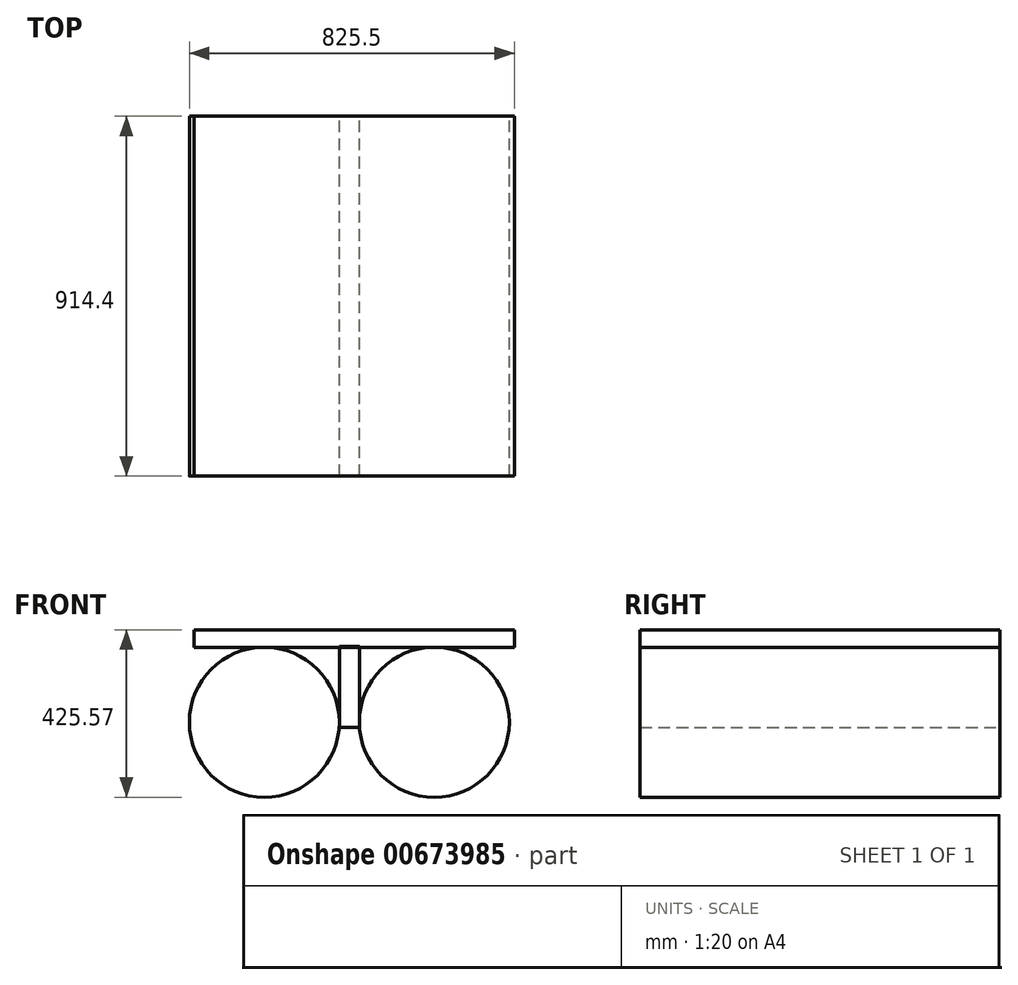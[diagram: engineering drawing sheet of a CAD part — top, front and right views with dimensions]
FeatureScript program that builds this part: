
annotation { "Feature Type Name" : "Feature", "Feature Type Description" : "" }
export const myFeature = defineFeature(function(context is Context, id is Id, definition is map)
    precondition{}
    {
        {
            var Q0;
            Q0=qCreatedBy(makeId("Front.planeOp"),FACE);
            var sketch = newSketch(context, id + "F0", { "sketchPlane" : qUnion([Q0])});
            skLineSegment(sketch, "E0.bottom", {"start": v(-192.12, 42.29) * mm, "end": v(620.68, 42.29) * mm});
            skLineSegment(sketch, "E0.top", {"start": v(-192.12, -2.28) * mm, "end": v(620.68, -2.28) * mm});
            skLineSegment(sketch, "E0.left", {"start": v(-192.12, 42.29) * mm, "end": v(-192.12, -2.28) * mm});
            skLineSegment(sketch, "E0.right", {"start": v(620.68, 42.29) * mm, "end": v(620.68, -2.28) * mm});
            skCircle(sketch, "E1", {"center": v(417.48, -192.78) * mm, "radius": 190.5 * mm});
            skSolve(sketch);
        }
        {
            var Q0;
            Q0=qCreatedBy(makeId("Front.planeOp"),FACE);
            var sketch = newSketch(context, id + "F1", { "sketchPlane" : qUnion([Q0])});
            skLineSegment(sketch, "E2.bottom", {"start": v(226.98, 0) * mm, "end": v(176.18, 0) * mm});
            skLineSegment(sketch, "E2.top", {"start": v(226.98, -205.48) * mm, "end": v(176.18, -205.48) * mm});
            skLineSegment(sketch, "E2.left", {"start": v(226.98, 0) * mm, "end": v(226.98, -205.48) * mm});
            skLineSegment(sketch, "E2.right", {"start": v(176.18, 0) * mm, "end": v(176.18, -205.48) * mm});
            skSolve(sketch);
        }
        {
            var Q0;
            Q0=qCreatedBy(makeId("Front.planeOp"),FACE);
            var sketch = newSketch(context, id + "F2", { "sketchPlane" : qUnion([Q0])});
            skCircle(sketch, "E3", {"center": v(-14.32, -192.78) * mm, "radius": 190.5 * mm});
            skSolve(sketch);
        }
        {
            var Q0;
            Q0 = qSketchRegion(id + "F0", true);
            var Q1;
            Q1=makeQuery(id+"F2.imprint","IMPRINT",FACE,{"disambiguationData":[TD([[makeQuery(id+"F2.imprint","IMPRINT",EDGE,{"derivedFrom":sQuery(id+"F2.wireOp",EDGE,"E3")}),1.0]])]});
            var Q2;
            Q2=makeQuery(id+"F1.imprint","IMPRINT",FACE,{"disambiguationData":[TD([[makeQuery(id+"F1.imprint","IMPRINT",EDGE,{"derivedFrom":sQuery(id+"F1.wireOp",EDGE,"E2.bottom")}),1.0]])]});
            extrude(context, id + "F3", {"entities" : qUnion([Q0, Q1, Q2]), "depth" : 914.4 * mm, "offsetDistance" : 25.4 * mm});
        }
    });
